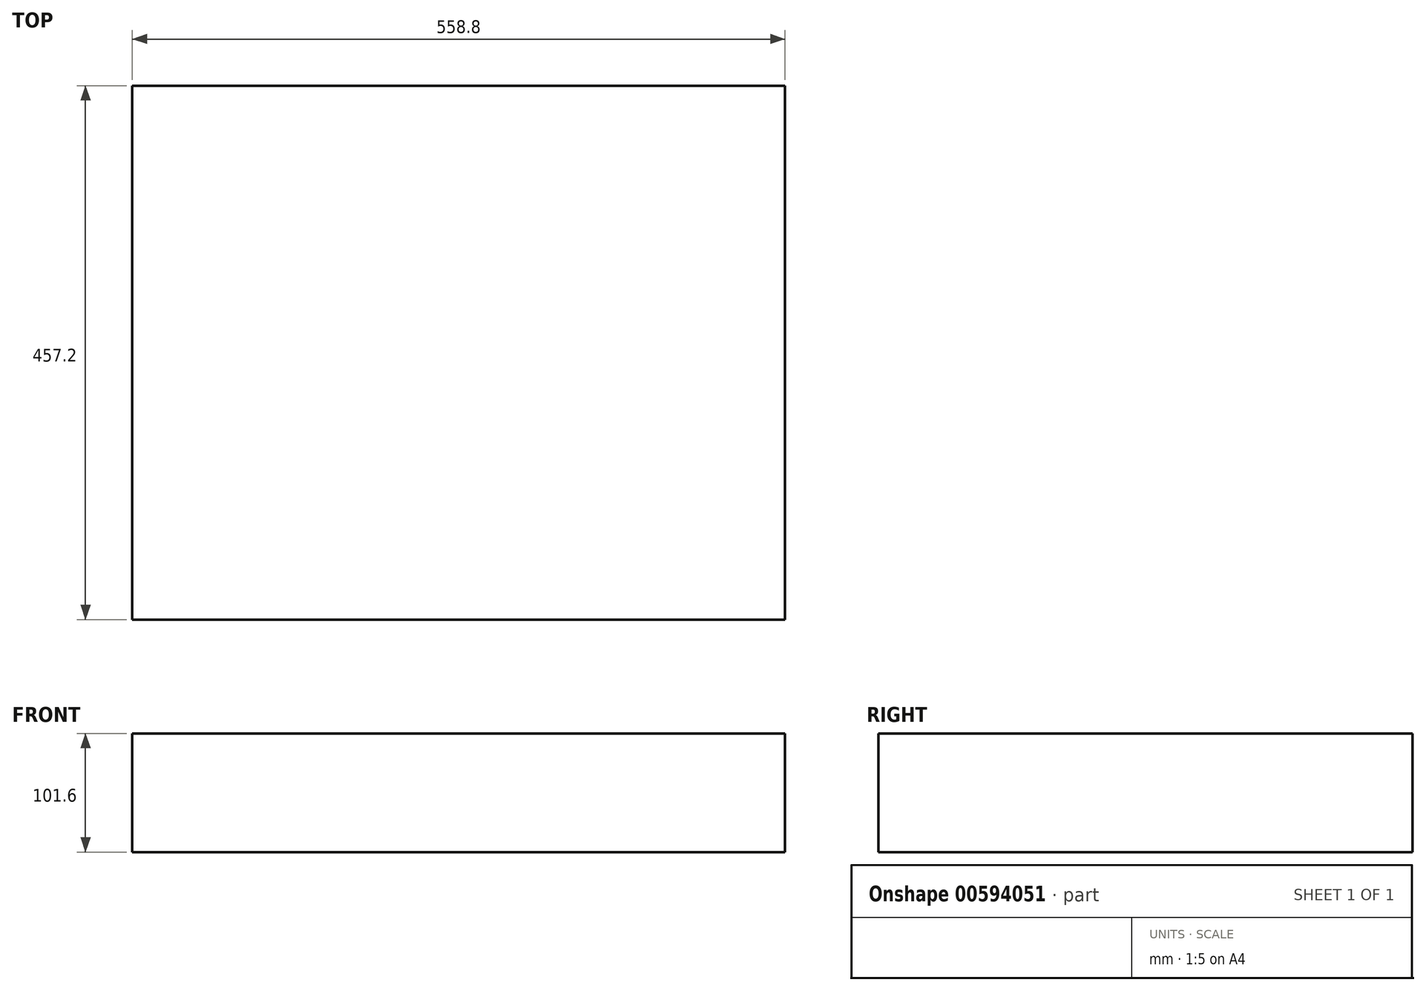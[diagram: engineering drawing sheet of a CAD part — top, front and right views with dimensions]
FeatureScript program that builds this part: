
annotation { "Feature Type Name" : "Feature", "Feature Type Description" : "" }
export const myFeature = defineFeature(function(context is Context, id is Id, definition is map)
    precondition{}
    {
        {
            var Q0;
            Q0=qCreatedBy(makeId("Front.planeOp"),FACE);
            var sketch = newSketch(context, id + "F0", { "sketchPlane" : qUnion([Q0])});
            skLineSegment(sketch, "E0.bottom", {"start": v(-270.32, -28.35) * mm, "end": v(288.48, -28.35) * mm});
            skLineSegment(sketch, "E0.top", {"start": v(-270.32, -129.95) * mm, "end": v(288.48, -129.95) * mm});
            skLineSegment(sketch, "E0.left", {"start": v(-270.32, -28.35) * mm, "end": v(-270.32, -129.95) * mm});
            skLineSegment(sketch, "E0.right", {"start": v(288.48, -28.35) * mm, "end": v(288.48, -129.95) * mm});
            skSolve(sketch);
        }
        {
            var Q0;
            Q0 = qSketchRegion(id + "F0", true);
            extrude(context, id + "F1", {"entities" : qUnion([Q0]), "oppositeDirection" : true, "depth" : 457.2 * mm, "offsetDistance" : 25.4 * mm});
        }
    });
